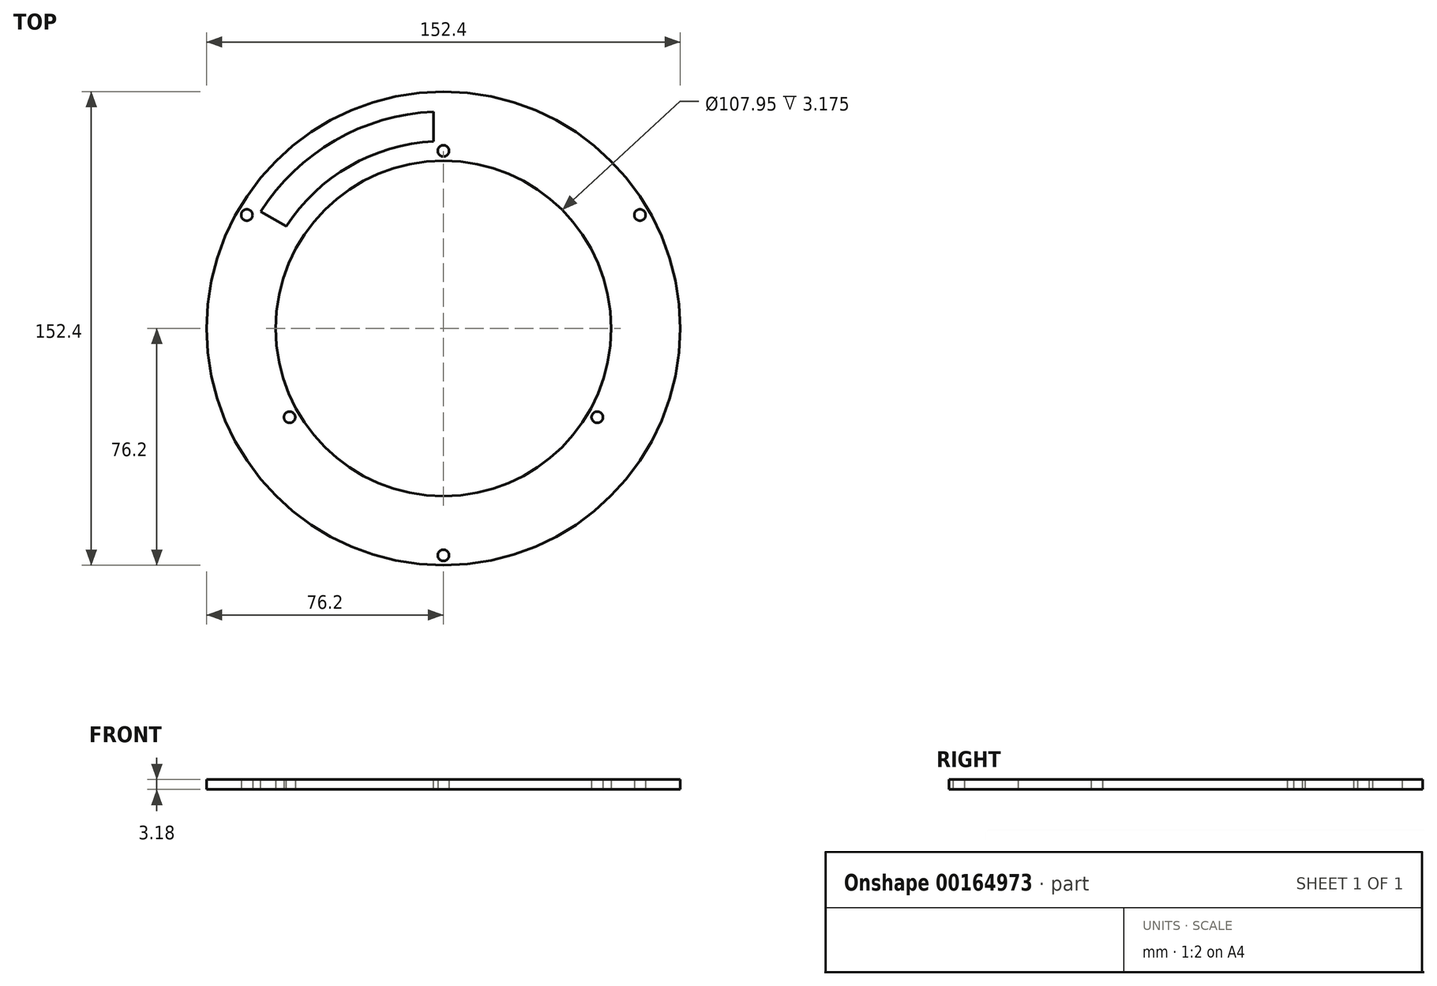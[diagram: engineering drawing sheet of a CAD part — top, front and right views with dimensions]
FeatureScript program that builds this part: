
annotation { "Feature Type Name" : "Feature", "Feature Type Description" : "" }
export const myFeature = defineFeature(function(context is Context, id is Id, definition is map)
    precondition{}
    {
        {
            var Q0;
            Q0=qCreatedBy(makeId("Top.planeOp"),FACE);
            var sketch = newSketch(context, id + "F0", { "sketchPlane" : qUnion([Q0])});
            skCircle(sketch, "E0", {"center": v(0, 0) * mm, "radius": 53.98 * mm});
            skCircle(sketch, "E1", {"center": v(0, 0) * mm, "radius": 76.2 * mm});
            skCircle(sketch, "E2.cCircle", {"center": v(0, 0) * mm, "radius": 36.51 * mm, "construction": true});
            skLineSegment(sketch, "E2.0", {"start": v(-63.24, 36.51) * mm, "end": v(63.24, 36.51) * mm, "construction": true});
            skLineSegment(sketch, "E2.1", {"start": v(63.24, 36.51) * mm, "end": v(0, -73.03) * mm, "construction": true});
            skLineSegment(sketch, "E2.2", {"start": v(0, -73.03) * mm, "end": v(-63.24, 36.51) * mm, "construction": true});
            skPoint(sketch, "E2.0.midPoint", {"position": v(0, 36.51) * mm});
            skCircle(sketch, "E3", {"center": v(0, -73.03) * mm, "radius": 3.18 * mm, "construction": true});
            skCircle(sketch, "E4", {"center": v(0, -73.03) * mm, "radius": 1.83 * mm});
            skCircle(sketch, "E5", {"center": v(63.24, 36.51) * mm, "radius": 1.83 * mm});
            skCircle(sketch, "E6", {"center": v(-63.24, 36.51) * mm, "radius": 1.83 * mm});
            skCircle(sketch, "E7.cCircle", {"center": v(0, 0) * mm, "radius": 28.57 * mm, "construction": true});
            skLineSegment(sketch, "E7.0", {"start": v(49.5, -28.57) * mm, "end": v(-49.5, -28.57) * mm, "construction": true});
            skLineSegment(sketch, "E7.1", {"start": v(-49.5, -28.58) * mm, "end": v(0, 57.15) * mm, "construction": true});
            skLineSegment(sketch, "E7.2", {"start": v(0, 57.15) * mm, "end": v(49.5, -28.58) * mm, "construction": true});
            skCircle(sketch, "E8", {"center": v(0, 57.15) * mm, "radius": 3.18 * mm, "construction": true});
            skCircle(sketch, "E9", {"center": v(-49.5, -28.57) * mm, "radius": 1.83 * mm});
            skCircle(sketch, "E10", {"center": v(0, 57.15) * mm, "radius": 1.83 * mm});
            skCircle(sketch, "E11", {"center": v(49.5, -28.57) * mm, "radius": 1.83 * mm});
            skSolve(sketch);
        }
        {
            var Q0;
            Q0=qSketchRegion(id+"F0",true);
            extrude(context, id + "F1", {"entities" : qUnion([Q0]), "depth" : 3.17 * mm});
        }
        {
            var Q0;
            Q0=makeQuery(id+"F1.opExtrude","CAP_FACE",FACE,{"disambiguationData":[OSD([sQuery(id+"F0.wireOp",EDGE,"E0"),sQuery(id+"F0.wireOp",EDGE,"E1"),sQuery(id+"F0.wireOp",EDGE,"E4"),sQuery(id+"F0.wireOp",EDGE,"E5"),sQuery(id+"F0.wireOp",EDGE,"E6"),sQuery(id+"F0.wireOp",EDGE,"E9"),sQuery(id+"F0.wireOp",EDGE,"E10"),sQuery(id+"F0.wireOp",EDGE,"E11")])],"isStart":false});
            var sketch = newSketch(context, id + "F2", { "sketchPlane" : qUnion([Q0])});
            skLineSegment(sketch, "E12", {"start": v(0, 0) * mm, "end": v(0, 57.15) * mm, "construction": true});
            skLineSegment(sketch, "E13", {"start": v(0, 57.15) * mm, "end": v(-3.18, 57.15) * mm, "construction": true});
            skLineSegment(sketch, "E14", {"start": v(0, 0) * mm, "end": v(-63.24, 36.51) * mm, "construction": true});
            skLineSegment(sketch, "E15", {"start": v(-63.24, 36.51) * mm, "end": v(-61.65, 39.26) * mm, "construction": true});
            skLineSegment(sketch, "E16", {"start": v(-61.65, 39.26) * mm, "end": v(-58.84, 37.64) * mm, "construction": true});
            skLineSegment(sketch, "E17", {"start": v(-3.18, 57.15) * mm, "end": v(-3.18, 60.24) * mm, "construction": true});
            skArc(sketch, "E18", {"start": v(-3.18, 69.78) * mm, "mid": v(-34.93, 60.5) * mm, "end": v(-58.84, 37.64) * mm});
            skArc(sketch, "E19", {"start": v(-3.17, 60.24) * mm, "mid": v(-30.16, 52.24) * mm, "end": v(-50.58, 32.87) * mm});
            skLineSegment(sketch, "E20", {"start": v(-58.84, 37.64) * mm, "end": v(-50.58, 32.87) * mm});
            skLineSegment(sketch, "E21", {"start": v(-3.17, 60.24) * mm, "end": v(-3.17, 69.78) * mm});
            skSolve(sketch);
        }
        {
            var Q0;
            Q0 = qSketchRegion(id + "F2", true);
            var Q1;
            Q1=makeQuery(id+"F1.opExtrude","CAP_FACE",FACE,{"disambiguationData":[OSD([sQuery(id+"F0.wireOp",EDGE,"E0"),sQuery(id+"F0.wireOp",EDGE,"E1"),sQuery(id+"F0.wireOp",EDGE,"E4"),sQuery(id+"F0.wireOp",EDGE,"E5"),sQuery(id+"F0.wireOp",EDGE,"E6"),sQuery(id+"F0.wireOp",EDGE,"E9"),sQuery(id+"F0.wireOp",EDGE,"E10"),sQuery(id+"F0.wireOp",EDGE,"E11")])],"isStart":true});
            extrude(context, id + "F3", {"entities" : qUnion([Q0]), "operationType" : NewBodyOperationType.REMOVE, "endBound" : BoundingType.UP_TO_SURFACE, "oppositeDirection" : true, "endBoundEntityFace" : qUnion([Q1]), "depth" : 25.4 * mm});
        }
    });
